# Revit family: T-Lasche 90° gewinkelt VA
name_source: partatom
category: HLS-Bauteile
revit_build: Autodesk Revit 2017 (Build: 20190507_1515(x64)
units: mm (PartAtom-declared; Revit-internal decimal feet)

## family parameters
Arbeitsebenenbasiert = Ja
Beim Laden mit Abzugskörper schneiden = Nein
Bemaßung runder Anschluss = Durchmesser verwenden
Gemeinsam genutzt = Ja
Immer vertikal = Nein
Raumberechnungspunkt = Nein
Teiletyp = Normal

## types (2) — shared parameters
Breite Material = 45 - 110 mm
Fabrikat = MEFA
Firma = MEFA Befestigungs- und Montagesysteme GmbH
Gewicht = 0.42 kg
Gewicht pro Bauteil = 0.42 kg
Kurztext2 = 90 ° Schenkel 85 x 45 mm
Länge Schenkel 1 = 85 mm  [stored 0.278871 ft]
Länge Schenkel 2 = 45 mm  [stored 0.147638 ft]
Material = Edelstahl
Mengeneinheit = St
Profil = C-Profil
Profiltyp = 45
Stärke Material = 5 mm  [stored 0.0164042 ft]
Vorgabe-Ansicht = 1219 mm
Winkel = 90 °
vpe = 1 St
zero-valued in all types: Sicherheitsfaktor, max. Rohraußendurchmesser, min. Rohraußendurchmesser

## per-type parameters (varying)
| type | Artikelnummer | EAN | Kurztext1 |
| T-Lasche 90° gewinkelt, V2A | 0480687 | 4250928412843 | T-Lasche gewinkelt C-Profil 45 V2A |
| T-Lasche 90° gewinkelt, V4A | 0481687 | 4250928413147 | T-Lasche gewinkelt C-Profil 45 V4A |

note: [stored X ft] marks values corroborated as IEEE doubles in the binary element streams (Revit-internal decimal feet)
